# Revit family: MixerSet_Wall_Nero_Celia_Basin_Bath
name_source: partatom
category: Plumbing Fixtures
units: mm (PartAtom-declared; Revit-internal decimal feet)

## family parameters
Always vertical = Yes
Cut with Voids When Loaded = Yes
Maintain Annotation Orientation = No
OmniClass Number = 23.31.11.19
OmniClass Title = Faucet Mixing Valves
Part Type = Normal
Room Calculation Point = No
Round Connector Dimension = Use Diameter
Shared = No
Work Plane-Based = No

## types (6) — shared parameters
CW Connection = Yes
HW Connection = Yes
IfcExportType = FAUCET
Manufacturer = Nero
ManufacturerOverallDepth = 204 mm
ManufacturerOverallHeight = 124 mm
ManufacturerOverallWidth = 200 mm  [stored 0.656168 ft]
ManufacturerURLProductSpecific = https://nerotapware.com.au
ModifiedIssue = 20240428 $
URL = https://nerotapware.com.au
Vent Connection = No
Waste Connection = No
zero-valued in all types: Default Elevation

## per-type parameters (varying)
| type | Assembly Code | BodyMaterial | Description | IfcExportAs | ManufacturerSpecCode | Model | Type Comments | Uniclass2015Code | Uniclass2015Title | Uniclass2015Version |
| Brushed Nickel (NR301507aBN) | C1030210 | Metal_Nickel_Nero_Brushed | Celia Wall Basin/Bath Mixer Brushed Nickel | ifcValve | NR301507aBN | NR301507aBN | Mixer Set - Wall - Basin - Bath - Brushed Nickel | Pr_40_20_87_55 | Mixer taps | Products v1.28 |
| Matte Black (NR301507aMB) | C1030210 | Metal_MatteBlack_Nero | Celia Wall Basin/Bath Mixer Matte Black | ifcValve | NR301507aMB | NR301507aMB | Mixer Set - Wall - Basin - Bath - Matte Black | Pr_40_20_87_55 | Mixer taps | Products v1.28 |
| Chrome (NR301507aCH) | C1030210 | Metal_Chrome_Nero | Celia Wall Basin/Bath Mixer Chrome | ifcValve | NR301507aCH | NR301507aCH | Mixer Set - Wall - Basin - Bath - Chrome | Pr_40_20_87_55 | Mixer taps | Products v1.28 |
| Matte Black (NR301510AMB) | D2010 | Metal_MatteBlack_Nero | Celia Wall Basin/Bath Mixer Matte Black | IfcValveType | NR301510AMB | NR301510AMB | Mixer Set - Wall - Basin - Bath - Matte Black | Pr_40_20_87 | Taps and water supply outlet fittings | Products v1.35 |
| Brushed Nickel (NR301510ABN) | D2010 | Metal_Nickel_Nero_Brushed | Celia Wall Basin/Bath Mixer Brushed Nickel | IfcValveType | NR301510ABN | NR301510ABN | Mixer Set - Wall - Basin - Bath - Brushed Nickel | Pr_40_20_87 | Taps and water supply outlet fittings | Products v1.35 |
| Chrome (NR301510ACH) | D2010 | Metal_Chrome_Nero | Celia Wall Basin/Bath Mixer Chrome | IfcValveType | NR301510ACH | NR301510ACH | Mixer Set - Wall - Basin - Bath - Chrome | Pr_40_20_87 | Taps and water supply outlet fittings | Products v1.35 |

note: [stored X ft] marks values corroborated as IEEE doubles in the binary element streams (Revit-internal decimal feet)

## geometry (parser evidence)
native form markers: Sweep x3
no freeform markers — native parametric forms only
